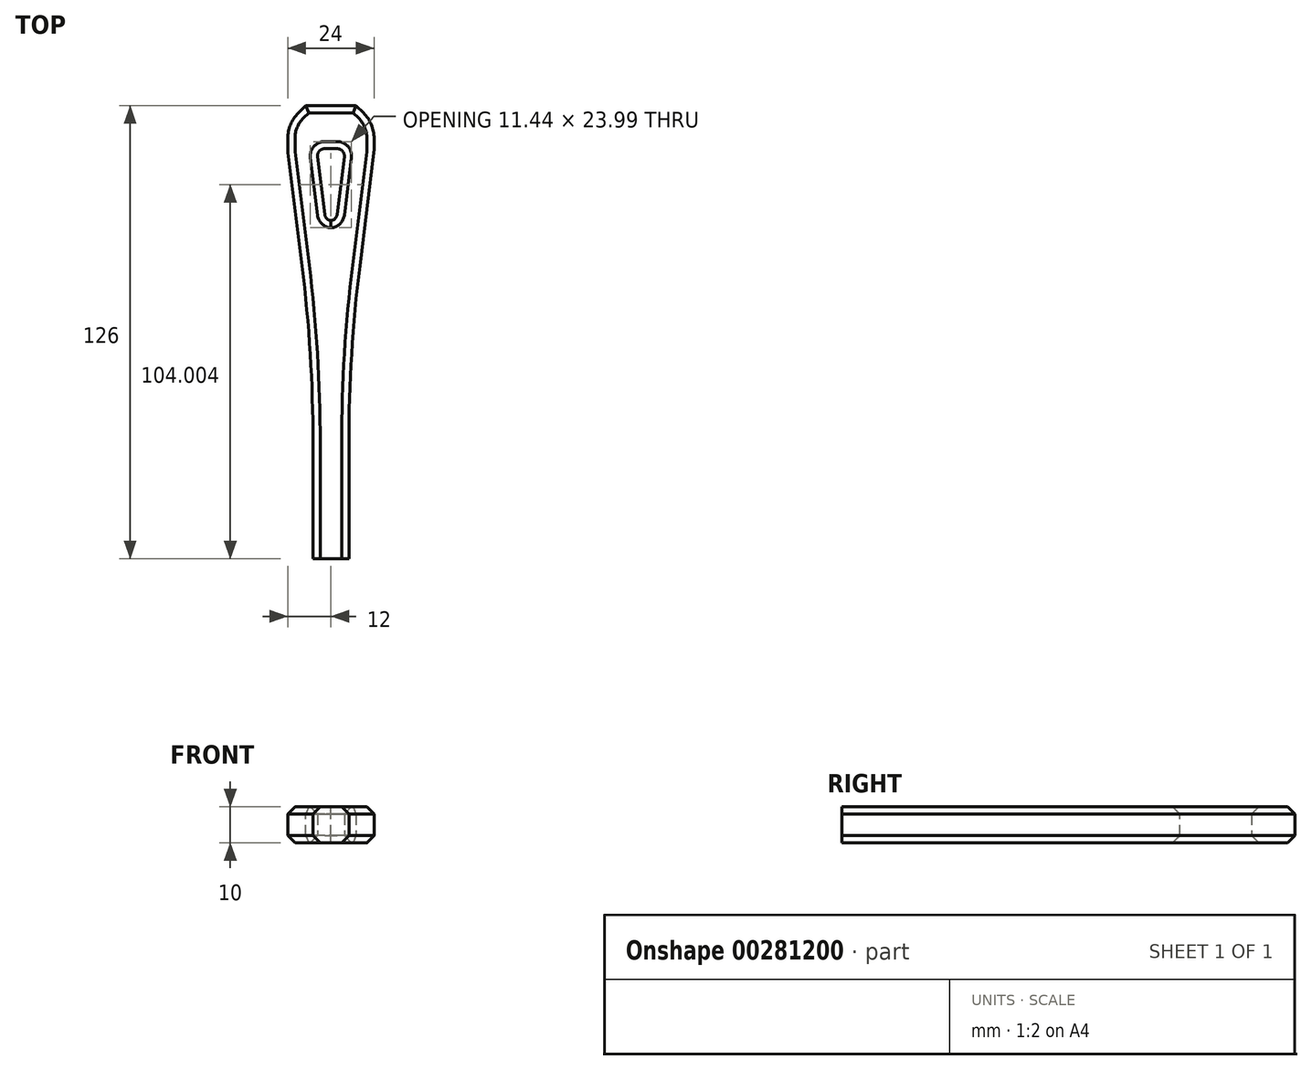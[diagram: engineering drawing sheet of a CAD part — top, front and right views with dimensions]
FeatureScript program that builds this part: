
annotation { "Feature Type Name" : "Feature", "Feature Type Description" : "" }
export const myFeature = defineFeature(function(context is Context, id is Id, definition is map)
    precondition{}
    {
        {
            var Q0;
            Q0=qCreatedBy(makeId("Top.planeOp"),FACE);
            var sketch = newSketch(context, id + "F0", { "sketchPlane" : qUnion([Q0])});
            skLineSegment(sketch, "E0.bottom", {"start": v(-1.52, 74) * mm, "end": v(1.52, 74) * mm});
            skLineSegment(sketch, "E0.top", {"start": v(-5, -20) * mm, "end": v(5, -20) * mm});
            skLineSegment(sketch, "E0.left", {"start": v(-5, 36.97) * mm, "end": v(-5, -20) * mm});
            skLineSegment(sketch, "E0.right", {"start": v(5, 36.97) * mm, "end": v(5, -20) * mm});
            skPoint(sketch, "E0.middle", {"position": v(0, 0) * mm});
            skLineSegment(sketch, "E1.bottom", {"start": v(-4, 106) * mm, "end": v(4, 106) * mm});
            skLineSegment(sketch, "E1.top", {"start": v(-4, 94) * mm, "end": v(4, 94) * mm});
            skLineSegment(sketch, "E1.left", {"start": v(-4, 106) * mm, "end": v(-4, 94) * mm});
            skLineSegment(sketch, "E1.right", {"start": v(4, 106) * mm, "end": v(4, 94) * mm});
            skPoint(sketch, "E1.middle", {"position": v(0, 100) * mm});
            skLineSegment(sketch, "E2", {"start": v(-4, 94) * mm, "end": v(-1.52, 74) * mm});
            skLineSegment(sketch, "E3", {"start": v(1.52, 74) * mm, "end": v(4, 94) * mm});
            skLineSegment(sketch, "E4", {"start": v(-5, 36.97) * mm, "end": v(-12, 93.5) * mm});
            skLineSegment(sketch, "E5", {"start": v(-12, 93.5) * mm, "end": v(-12, 106) * mm});
            skLineSegment(sketch, "E6", {"start": v(-12, 106) * mm, "end": v(-4, 106) * mm});
            skLineSegment(sketch, "E7.MirrorCS", {"start": v(5, 36.97) * mm, "end": v(12, 93.5) * mm});
            skLineSegment(sketch, "E8.MirrorCS", {"start": v(12, 106) * mm, "end": v(4, 106) * mm});
            skLineSegment(sketch, "E9.MirrorCS", {"start": v(12, 93.5) * mm, "end": v(12, 106) * mm});
            skLineSegment(sketch, "E10", {"start": v(-5, 0) * mm, "end": v(5, 0) * mm, "construction": true});
            skSolve(sketch);
        }
        {
            var Q0;
            Q0=makeQuery(id+"F0.imprint","IMPRINT",FACE,{"disambiguationData":[TD([[makeQuery(id+"F0.imprint","IMPRINT",EDGE,{"derivedFrom":sQuery(id+"F0.wireOp",EDGE,"E0.bottom")}),-1.0]])]});
            var Q1;
            Q1=makeQuery(id+"F0.imprint","IMPRINT",FACE,{"disambiguationData":[TD([[makeQuery(id+"F0.imprint","IMPRINT",EDGE,{"derivedFrom":sQuery(id+"F0.wireOp",EDGE,"E1.bottom")}),-1.0]])]});
            extrude(context, id + "F1", {"entities" : qUnion([Q0, Q1]), "depth" : 10 * mm});
        }
        {
            var Q0;
            Q0=makeQuery(id+"F1.opExtrude","SWEPT_EDGE",EDGE,{"disambiguationData":[OSD([sQuery(id+"F0.wireOp",EDGE,"E1.top"),sQuery(id+"F0.wireOp",EDGE,"E1.right"),sQuery(id+"F0.wireOp",EDGE,"E3")])]});
            var Q1;
            Q1=makeQuery(id+"F1.opExtrude","SWEPT_EDGE",EDGE,{"disambiguationData":[OSD([sQuery(id+"F0.wireOp",EDGE,"E1.top"),sQuery(id+"F0.wireOp",EDGE,"E1.left"),sQuery(id+"F0.wireOp",EDGE,"E2")])]});
            var Q2;
            Q2=makeQuery(id+"F1.opExtrude","SWEPT_EDGE",EDGE,{"disambiguationData":[OSD([sQuery(id+"F0.wireOp",EDGE,"E0.bottom"),sQuery(id+"F0.wireOp",EDGE,"E2")])]});
            var Q3;
            Q3=makeQuery(id+"F1.opExtrude","SWEPT_EDGE",EDGE,{"disambiguationData":[OSD([sQuery(id+"F0.wireOp",EDGE,"E0.bottom"),sQuery(id+"F0.wireOp",EDGE,"E3")])]});
            fillet(context, id + "F2", {"entities" : qUnion([Q0, Q1, Q2, Q3]), "radius" : 2 * mm, "tangentPropagation" : true, "allowEdgeOverflow" : false});
        }
        {
            var Q0;
            Q0=makeQuery(id+"F1.opExtrude","SWEPT_EDGE",EDGE,{"disambiguationData":[OSD([sQuery(id+"F0.wireOp",EDGE,"E5"),sQuery(id+"F0.wireOp",EDGE,"E6")])]});
            var Q1;
            Q1=makeQuery(id+"F1.opExtrude","SWEPT_EDGE",EDGE,{"disambiguationData":[OSD([sQuery(id+"F0.wireOp",EDGE,"E8.MirrorCS"),sQuery(id+"F0.wireOp",EDGE,"E9.MirrorCS")])]});
            chamfer(context, id + "F3", {"entities" : qUnion([Q0, Q1]), "width" : 5 * mm, "tangentPropagation" : true});
        }
        {
            var Q0;
            Q0=makeQuery(id+"F1.opExtrude","SWEPT_EDGE",EDGE,{"disambiguationData":[OSD([sQuery(id+"F0.wireOp",EDGE,"E0.right"),sQuery(id+"F0.wireOp",EDGE,"E7.MirrorCS")])]});
            var Q1;
            Q1=makeQuery(id+"F1.opExtrude","SWEPT_EDGE",EDGE,{"disambiguationData":[OSD([sQuery(id+"F0.wireOp",EDGE,"E0.left"),sQuery(id+"F0.wireOp",EDGE,"E4")])]});
            fillet(context, id + "F4", {"entities" : qUnion([Q0, Q1]), "radius" : 400 * mm, "tangentPropagation" : true, "allowEdgeOverflow" : false});
        }
        {
            var Q0;
            Q0=makeQuery(id+"F1.opExtrude","SWEPT_EDGE",EDGE,{"disambiguationData":[OSD([sQuery(id+"F0.wireOp",EDGE,"E4"),sQuery(id+"F0.wireOp",EDGE,"E5")])]});
            var Q1;
            {var subQ0=sQuery(id+"F0.wireOp",EDGE,"E5");Q1=makeQuery(id+"F3.opChamfer","BLEND_EDGE",EDGE,{"blendedFrom":[makeQuery(id+"F1.opExtrude","SWEPT_EDGE",EDGE,{"disambiguationData":[OSD([subQ0,sQuery(id+"F0.wireOp",EDGE,"E6")])]}),makeQuery(id+"F1.opExtrude","SWEPT_FACE",FACE,{"disambiguationData":[OSD([subQ0])]})],"blendedInto":[makeQuery(id+"F1.opExtrude","SWEPT_FACE",FACE,{"disambiguationData":[OSD([subQ0])]})]});}
            var Q2;
            {var subQ0=sQuery(id+"F0.wireOp",EDGE,"E9.MirrorCS");Q2=makeQuery(id+"F3.opChamfer","BLEND_EDGE",EDGE,{"blendedFrom":[makeQuery(id+"F1.opExtrude","SWEPT_EDGE",EDGE,{"disambiguationData":[OSD([sQuery(id+"F0.wireOp",EDGE,"E8.MirrorCS"),subQ0])]}),makeQuery(id+"F1.opExtrude","SWEPT_FACE",FACE,{"disambiguationData":[OSD([subQ0])]})],"blendedInto":[makeQuery(id+"F1.opExtrude","SWEPT_FACE",FACE,{"disambiguationData":[OSD([subQ0])]})]});}
            var Q3;
            Q3=makeQuery(id+"F1.opExtrude","SWEPT_EDGE",EDGE,{"disambiguationData":[OSD([sQuery(id+"F0.wireOp",EDGE,"E7.MirrorCS"),sQuery(id+"F0.wireOp",EDGE,"E9.MirrorCS")])]});
            fillet(context, id + "F5", {"entities" : qUnion([Q0, Q1, Q2, Q3]), "radius" : 10 * mm, "tangentPropagation" : true, "allowEdgeOverflow" : false});
        }
        {
            var Q0;
            {var subQ0=sQuery(id+"F0.wireOp",EDGE,"E4");var subQ1=sQuery(id+"F0.wireOp",EDGE,"E0.left");Q0=makeQuery(id+"F4.opFillet","BLEND_EDGE",EDGE,{"blendedFrom":[makeQuery(id+"F1.opExtrude","SWEPT_EDGE",EDGE,{"disambiguationData":[OSD([subQ1,subQ0])]}),makeQuery(id+"F1.opExtrude","CAP_FACE",FACE,{"disambiguationData":[OSD([sQuery(id+"F0.wireOp",EDGE,"E0.bottom"),sQuery(id+"F0.wireOp",EDGE,"E0.top"),subQ1,sQuery(id+"F0.wireOp",EDGE,"E0.right"),sQuery(id+"F0.wireOp",EDGE,"E1.bottom"),sQuery(id+"F0.wireOp",EDGE,"E1.top"),sQuery(id+"F0.wireOp",EDGE,"E2"),sQuery(id+"F0.wireOp",EDGE,"E3"),subQ0,sQuery(id+"F0.wireOp",EDGE,"E5"),sQuery(id+"F0.wireOp",EDGE,"E6"),sQuery(id+"F0.wireOp",EDGE,"E7.MirrorCS"),sQuery(id+"F0.wireOp",EDGE,"E8.MirrorCS"),sQuery(id+"F0.wireOp",EDGE,"E9.MirrorCS")])],"isStart":false})],"blendedInto":[makeQuery(id+"F1.opExtrude","CAP_FACE",FACE,{"disambiguationData":[OSD([sQuery(id+"F0.wireOp",EDGE,"E0.bottom"),sQuery(id+"F0.wireOp",EDGE,"E0.top"),subQ1,sQuery(id+"F0.wireOp",EDGE,"E0.right"),sQuery(id+"F0.wireOp",EDGE,"E1.bottom"),sQuery(id+"F0.wireOp",EDGE,"E1.top"),sQuery(id+"F0.wireOp",EDGE,"E2"),sQuery(id+"F0.wireOp",EDGE,"E3"),subQ0,sQuery(id+"F0.wireOp",EDGE,"E5"),sQuery(id+"F0.wireOp",EDGE,"E6"),sQuery(id+"F0.wireOp",EDGE,"E7.MirrorCS"),sQuery(id+"F0.wireOp",EDGE,"E8.MirrorCS"),sQuery(id+"F0.wireOp",EDGE,"E9.MirrorCS")])],"isStart":false})]});}
            var Q1;
            {var subQ0=sQuery(id+"F0.wireOp",EDGE,"E7.MirrorCS");var subQ1=sQuery(id+"F0.wireOp",EDGE,"E0.right");Q1=makeQuery(id+"F4.opFillet","BLEND_EDGE",EDGE,{"blendedFrom":[makeQuery(id+"F1.opExtrude","SWEPT_EDGE",EDGE,{"disambiguationData":[OSD([subQ1,subQ0])]}),makeQuery(id+"F1.opExtrude","CAP_FACE",FACE,{"disambiguationData":[OSD([sQuery(id+"F0.wireOp",EDGE,"E0.bottom"),sQuery(id+"F0.wireOp",EDGE,"E0.top"),sQuery(id+"F0.wireOp",EDGE,"E0.left"),subQ1,sQuery(id+"F0.wireOp",EDGE,"E1.bottom"),sQuery(id+"F0.wireOp",EDGE,"E1.top"),sQuery(id+"F0.wireOp",EDGE,"E2"),sQuery(id+"F0.wireOp",EDGE,"E3"),sQuery(id+"F0.wireOp",EDGE,"E4"),sQuery(id+"F0.wireOp",EDGE,"E5"),sQuery(id+"F0.wireOp",EDGE,"E6"),subQ0,sQuery(id+"F0.wireOp",EDGE,"E8.MirrorCS"),sQuery(id+"F0.wireOp",EDGE,"E9.MirrorCS")])],"isStart":false})],"blendedInto":[makeQuery(id+"F1.opExtrude","CAP_FACE",FACE,{"disambiguationData":[OSD([sQuery(id+"F0.wireOp",EDGE,"E0.bottom"),sQuery(id+"F0.wireOp",EDGE,"E0.top"),sQuery(id+"F0.wireOp",EDGE,"E0.left"),subQ1,sQuery(id+"F0.wireOp",EDGE,"E1.bottom"),sQuery(id+"F0.wireOp",EDGE,"E1.top"),sQuery(id+"F0.wireOp",EDGE,"E2"),sQuery(id+"F0.wireOp",EDGE,"E3"),sQuery(id+"F0.wireOp",EDGE,"E4"),sQuery(id+"F0.wireOp",EDGE,"E5"),sQuery(id+"F0.wireOp",EDGE,"E6"),subQ0,sQuery(id+"F0.wireOp",EDGE,"E8.MirrorCS"),sQuery(id+"F0.wireOp",EDGE,"E9.MirrorCS")])],"isStart":false})]});}
            var Q2;
            {var subQ0=sQuery(id+"F0.wireOp",EDGE,"E4");var subQ1=sQuery(id+"F0.wireOp",EDGE,"E0.left");Q2=makeQuery(id+"F4.opFillet","BLEND_EDGE",EDGE,{"blendedFrom":[makeQuery(id+"F1.opExtrude","SWEPT_EDGE",EDGE,{"disambiguationData":[OSD([subQ1,subQ0])]}),makeQuery(id+"F1.opExtrude","CAP_FACE",FACE,{"disambiguationData":[OSD([sQuery(id+"F0.wireOp",EDGE,"E0.bottom"),sQuery(id+"F0.wireOp",EDGE,"E0.top"),subQ1,sQuery(id+"F0.wireOp",EDGE,"E0.right"),sQuery(id+"F0.wireOp",EDGE,"E1.bottom"),sQuery(id+"F0.wireOp",EDGE,"E1.top"),sQuery(id+"F0.wireOp",EDGE,"E2"),sQuery(id+"F0.wireOp",EDGE,"E3"),subQ0,sQuery(id+"F0.wireOp",EDGE,"E5"),sQuery(id+"F0.wireOp",EDGE,"E6"),sQuery(id+"F0.wireOp",EDGE,"E7.MirrorCS"),sQuery(id+"F0.wireOp",EDGE,"E8.MirrorCS"),sQuery(id+"F0.wireOp",EDGE,"E9.MirrorCS")])],"isStart":true})],"blendedInto":[makeQuery(id+"F1.opExtrude","CAP_FACE",FACE,{"disambiguationData":[OSD([sQuery(id+"F0.wireOp",EDGE,"E0.bottom"),sQuery(id+"F0.wireOp",EDGE,"E0.top"),subQ1,sQuery(id+"F0.wireOp",EDGE,"E0.right"),sQuery(id+"F0.wireOp",EDGE,"E1.bottom"),sQuery(id+"F0.wireOp",EDGE,"E1.top"),sQuery(id+"F0.wireOp",EDGE,"E2"),sQuery(id+"F0.wireOp",EDGE,"E3"),subQ0,sQuery(id+"F0.wireOp",EDGE,"E5"),sQuery(id+"F0.wireOp",EDGE,"E6"),sQuery(id+"F0.wireOp",EDGE,"E7.MirrorCS"),sQuery(id+"F0.wireOp",EDGE,"E8.MirrorCS"),sQuery(id+"F0.wireOp",EDGE,"E9.MirrorCS")])],"isStart":true})]});}
            var Q3;
            {var subQ0=sQuery(id+"F0.wireOp",EDGE,"E7.MirrorCS");var subQ1=sQuery(id+"F0.wireOp",EDGE,"E0.right");Q3=makeQuery(id+"F4.opFillet","BLEND_EDGE",EDGE,{"blendedFrom":[makeQuery(id+"F1.opExtrude","SWEPT_EDGE",EDGE,{"disambiguationData":[OSD([subQ1,subQ0])]}),makeQuery(id+"F1.opExtrude","CAP_FACE",FACE,{"disambiguationData":[OSD([sQuery(id+"F0.wireOp",EDGE,"E0.bottom"),sQuery(id+"F0.wireOp",EDGE,"E0.top"),sQuery(id+"F0.wireOp",EDGE,"E0.left"),subQ1,sQuery(id+"F0.wireOp",EDGE,"E1.bottom"),sQuery(id+"F0.wireOp",EDGE,"E1.top"),sQuery(id+"F0.wireOp",EDGE,"E2"),sQuery(id+"F0.wireOp",EDGE,"E3"),sQuery(id+"F0.wireOp",EDGE,"E4"),sQuery(id+"F0.wireOp",EDGE,"E5"),sQuery(id+"F0.wireOp",EDGE,"E6"),subQ0,sQuery(id+"F0.wireOp",EDGE,"E8.MirrorCS"),sQuery(id+"F0.wireOp",EDGE,"E9.MirrorCS")])],"isStart":true})],"blendedInto":[makeQuery(id+"F1.opExtrude","CAP_FACE",FACE,{"disambiguationData":[OSD([sQuery(id+"F0.wireOp",EDGE,"E0.bottom"),sQuery(id+"F0.wireOp",EDGE,"E0.top"),sQuery(id+"F0.wireOp",EDGE,"E0.left"),subQ1,sQuery(id+"F0.wireOp",EDGE,"E1.bottom"),sQuery(id+"F0.wireOp",EDGE,"E1.top"),sQuery(id+"F0.wireOp",EDGE,"E2"),sQuery(id+"F0.wireOp",EDGE,"E3"),sQuery(id+"F0.wireOp",EDGE,"E4"),sQuery(id+"F0.wireOp",EDGE,"E5"),sQuery(id+"F0.wireOp",EDGE,"E6"),subQ0,sQuery(id+"F0.wireOp",EDGE,"E8.MirrorCS"),sQuery(id+"F0.wireOp",EDGE,"E9.MirrorCS")])],"isStart":true})]});}
            var Q4;
            Q4=makeQuery(id+"F1.opExtrude","CAP_EDGE",EDGE,{"disambiguationData":[OSD([sQuery(id+"F0.wireOp",EDGE,"E1.top")])],"isStart":false});
            var Q5;
            Q5=makeQuery(id+"F1.opExtrude","CAP_EDGE",EDGE,{"disambiguationData":[OSD([sQuery(id+"F0.wireOp",EDGE,"E1.bottom"),sQuery(id+"F0.wireOp",EDGE,"E6"),sQuery(id+"F0.wireOp",EDGE,"E8.MirrorCS")])],"isStart":false});
            var Q6;
            Q6=makeQuery(id+"F1.opExtrude","CAP_EDGE",EDGE,{"disambiguationData":[OSD([sQuery(id+"F0.wireOp",EDGE,"E1.top")])],"isStart":true});
            var Q7;
            Q7=makeQuery(id+"F1.opExtrude","CAP_EDGE",EDGE,{"disambiguationData":[OSD([sQuery(id+"F0.wireOp",EDGE,"E1.bottom"),sQuery(id+"F0.wireOp",EDGE,"E6"),sQuery(id+"F0.wireOp",EDGE,"E8.MirrorCS")])],"isStart":true});
            var Q8;
            {var subQ0=sQuery(id+"F0.wireOp",EDGE,"E6");var subQ1=sQuery(id+"F0.wireOp",EDGE,"E5");Q8=makeQuery(id+"F3.opChamfer","BLEND_EDGE",EDGE,{"blendedFrom":[makeQuery(id+"F1.opExtrude","SWEPT_EDGE",EDGE,{"disambiguationData":[OSD([subQ1,subQ0])]}),makeQuery(id+"F1.opExtrude","CAP_FACE",FACE,{"disambiguationData":[OSD([sQuery(id+"F0.wireOp",EDGE,"E0.bottom"),sQuery(id+"F0.wireOp",EDGE,"E0.top"),sQuery(id+"F0.wireOp",EDGE,"E0.left"),sQuery(id+"F0.wireOp",EDGE,"E0.right"),sQuery(id+"F0.wireOp",EDGE,"E1.bottom"),sQuery(id+"F0.wireOp",EDGE,"E1.top"),sQuery(id+"F0.wireOp",EDGE,"E2"),sQuery(id+"F0.wireOp",EDGE,"E3"),sQuery(id+"F0.wireOp",EDGE,"E4"),subQ1,subQ0,sQuery(id+"F0.wireOp",EDGE,"E7.MirrorCS"),sQuery(id+"F0.wireOp",EDGE,"E8.MirrorCS"),sQuery(id+"F0.wireOp",EDGE,"E9.MirrorCS")])],"isStart":false})],"blendedInto":[makeQuery(id+"F1.opExtrude","CAP_FACE",FACE,{"disambiguationData":[OSD([sQuery(id+"F0.wireOp",EDGE,"E0.bottom"),sQuery(id+"F0.wireOp",EDGE,"E0.top"),sQuery(id+"F0.wireOp",EDGE,"E0.left"),sQuery(id+"F0.wireOp",EDGE,"E0.right"),sQuery(id+"F0.wireOp",EDGE,"E1.bottom"),sQuery(id+"F0.wireOp",EDGE,"E1.top"),sQuery(id+"F0.wireOp",EDGE,"E2"),sQuery(id+"F0.wireOp",EDGE,"E3"),sQuery(id+"F0.wireOp",EDGE,"E4"),subQ1,subQ0,sQuery(id+"F0.wireOp",EDGE,"E7.MirrorCS"),sQuery(id+"F0.wireOp",EDGE,"E8.MirrorCS"),sQuery(id+"F0.wireOp",EDGE,"E9.MirrorCS")])],"isStart":false})]});}
            var Q9;
            {var subQ0=sQuery(id+"F0.wireOp",EDGE,"E6");var subQ1=sQuery(id+"F0.wireOp",EDGE,"E5");Q9=makeQuery(id+"F3.opChamfer","BLEND_EDGE",EDGE,{"blendedFrom":[makeQuery(id+"F1.opExtrude","SWEPT_EDGE",EDGE,{"disambiguationData":[OSD([subQ1,subQ0])]}),makeQuery(id+"F1.opExtrude","CAP_FACE",FACE,{"disambiguationData":[OSD([sQuery(id+"F0.wireOp",EDGE,"E0.bottom"),sQuery(id+"F0.wireOp",EDGE,"E0.top"),sQuery(id+"F0.wireOp",EDGE,"E0.left"),sQuery(id+"F0.wireOp",EDGE,"E0.right"),sQuery(id+"F0.wireOp",EDGE,"E1.bottom"),sQuery(id+"F0.wireOp",EDGE,"E1.top"),sQuery(id+"F0.wireOp",EDGE,"E2"),sQuery(id+"F0.wireOp",EDGE,"E3"),sQuery(id+"F0.wireOp",EDGE,"E4"),subQ1,subQ0,sQuery(id+"F0.wireOp",EDGE,"E7.MirrorCS"),sQuery(id+"F0.wireOp",EDGE,"E8.MirrorCS"),sQuery(id+"F0.wireOp",EDGE,"E9.MirrorCS")])],"isStart":true})],"blendedInto":[makeQuery(id+"F1.opExtrude","CAP_FACE",FACE,{"disambiguationData":[OSD([sQuery(id+"F0.wireOp",EDGE,"E0.bottom"),sQuery(id+"F0.wireOp",EDGE,"E0.top"),sQuery(id+"F0.wireOp",EDGE,"E0.left"),sQuery(id+"F0.wireOp",EDGE,"E0.right"),sQuery(id+"F0.wireOp",EDGE,"E1.bottom"),sQuery(id+"F0.wireOp",EDGE,"E1.top"),sQuery(id+"F0.wireOp",EDGE,"E2"),sQuery(id+"F0.wireOp",EDGE,"E3"),sQuery(id+"F0.wireOp",EDGE,"E4"),subQ1,subQ0,sQuery(id+"F0.wireOp",EDGE,"E7.MirrorCS"),sQuery(id+"F0.wireOp",EDGE,"E8.MirrorCS"),sQuery(id+"F0.wireOp",EDGE,"E9.MirrorCS")])],"isStart":true})]});}
            var Q10;
            {var subQ0=sQuery(id+"F0.wireOp",EDGE,"E9.MirrorCS");var subQ1=sQuery(id+"F0.wireOp",EDGE,"E8.MirrorCS");Q10=makeQuery(id+"F3.opChamfer","BLEND_EDGE",EDGE,{"blendedFrom":[makeQuery(id+"F1.opExtrude","SWEPT_EDGE",EDGE,{"disambiguationData":[OSD([subQ1,subQ0])]}),makeQuery(id+"F1.opExtrude","CAP_FACE",FACE,{"disambiguationData":[OSD([sQuery(id+"F0.wireOp",EDGE,"E0.bottom"),sQuery(id+"F0.wireOp",EDGE,"E0.top"),sQuery(id+"F0.wireOp",EDGE,"E0.left"),sQuery(id+"F0.wireOp",EDGE,"E0.right"),sQuery(id+"F0.wireOp",EDGE,"E1.bottom"),sQuery(id+"F0.wireOp",EDGE,"E1.top"),sQuery(id+"F0.wireOp",EDGE,"E2"),sQuery(id+"F0.wireOp",EDGE,"E3"),sQuery(id+"F0.wireOp",EDGE,"E4"),sQuery(id+"F0.wireOp",EDGE,"E5"),sQuery(id+"F0.wireOp",EDGE,"E6"),sQuery(id+"F0.wireOp",EDGE,"E7.MirrorCS"),subQ1,subQ0])],"isStart":false})],"blendedInto":[makeQuery(id+"F1.opExtrude","CAP_FACE",FACE,{"disambiguationData":[OSD([sQuery(id+"F0.wireOp",EDGE,"E0.bottom"),sQuery(id+"F0.wireOp",EDGE,"E0.top"),sQuery(id+"F0.wireOp",EDGE,"E0.left"),sQuery(id+"F0.wireOp",EDGE,"E0.right"),sQuery(id+"F0.wireOp",EDGE,"E1.bottom"),sQuery(id+"F0.wireOp",EDGE,"E1.top"),sQuery(id+"F0.wireOp",EDGE,"E2"),sQuery(id+"F0.wireOp",EDGE,"E3"),sQuery(id+"F0.wireOp",EDGE,"E4"),sQuery(id+"F0.wireOp",EDGE,"E5"),sQuery(id+"F0.wireOp",EDGE,"E6"),sQuery(id+"F0.wireOp",EDGE,"E7.MirrorCS"),subQ1,subQ0])],"isStart":false})]});}
            var Q11;
            {var subQ0=sQuery(id+"F0.wireOp",EDGE,"E9.MirrorCS");var subQ1=sQuery(id+"F0.wireOp",EDGE,"E8.MirrorCS");Q11=makeQuery(id+"F3.opChamfer","BLEND_EDGE",EDGE,{"blendedFrom":[makeQuery(id+"F1.opExtrude","SWEPT_EDGE",EDGE,{"disambiguationData":[OSD([subQ1,subQ0])]}),makeQuery(id+"F1.opExtrude","CAP_FACE",FACE,{"disambiguationData":[OSD([sQuery(id+"F0.wireOp",EDGE,"E0.bottom"),sQuery(id+"F0.wireOp",EDGE,"E0.top"),sQuery(id+"F0.wireOp",EDGE,"E0.left"),sQuery(id+"F0.wireOp",EDGE,"E0.right"),sQuery(id+"F0.wireOp",EDGE,"E1.bottom"),sQuery(id+"F0.wireOp",EDGE,"E1.top"),sQuery(id+"F0.wireOp",EDGE,"E2"),sQuery(id+"F0.wireOp",EDGE,"E3"),sQuery(id+"F0.wireOp",EDGE,"E4"),sQuery(id+"F0.wireOp",EDGE,"E5"),sQuery(id+"F0.wireOp",EDGE,"E6"),sQuery(id+"F0.wireOp",EDGE,"E7.MirrorCS"),subQ1,subQ0])],"isStart":true})],"blendedInto":[makeQuery(id+"F1.opExtrude","CAP_FACE",FACE,{"disambiguationData":[OSD([sQuery(id+"F0.wireOp",EDGE,"E0.bottom"),sQuery(id+"F0.wireOp",EDGE,"E0.top"),sQuery(id+"F0.wireOp",EDGE,"E0.left"),sQuery(id+"F0.wireOp",EDGE,"E0.right"),sQuery(id+"F0.wireOp",EDGE,"E1.bottom"),sQuery(id+"F0.wireOp",EDGE,"E1.top"),sQuery(id+"F0.wireOp",EDGE,"E2"),sQuery(id+"F0.wireOp",EDGE,"E3"),sQuery(id+"F0.wireOp",EDGE,"E4"),sQuery(id+"F0.wireOp",EDGE,"E5"),sQuery(id+"F0.wireOp",EDGE,"E6"),sQuery(id+"F0.wireOp",EDGE,"E7.MirrorCS"),subQ1,subQ0])],"isStart":true})]});}
            var Q12;
            Q12=makeQuery(id+"F1.opExtrude","CAP_EDGE",EDGE,{"disambiguationData":[OSD([sQuery(id+"F0.wireOp",EDGE,"E9.MirrorCS")])],"isStart":false});
            var Q13;
            Q13=makeQuery(id+"F1.opExtrude","CAP_EDGE",EDGE,{"disambiguationData":[OSD([sQuery(id+"F0.wireOp",EDGE,"E9.MirrorCS")])],"isStart":true});
            var Q14;
            Q14=makeQuery(id+"F1.opExtrude","CAP_EDGE",EDGE,{"disambiguationData":[OSD([sQuery(id+"F0.wireOp",EDGE,"E5")])],"isStart":false});
            var Q15;
            Q15=makeQuery(id+"F1.opExtrude","CAP_EDGE",EDGE,{"disambiguationData":[OSD([sQuery(id+"F0.wireOp",EDGE,"E5")])],"isStart":true});
            chamfer(context, id + "F6", {"entities" : qUnion([Q0, Q1, Q2, Q3, Q4, Q5, Q6, Q7, Q8, Q9, Q10, Q11, Q12, Q13, Q14, Q15]), "width" : 2 * mm, "tangentPropagation" : true});
        }
    });
